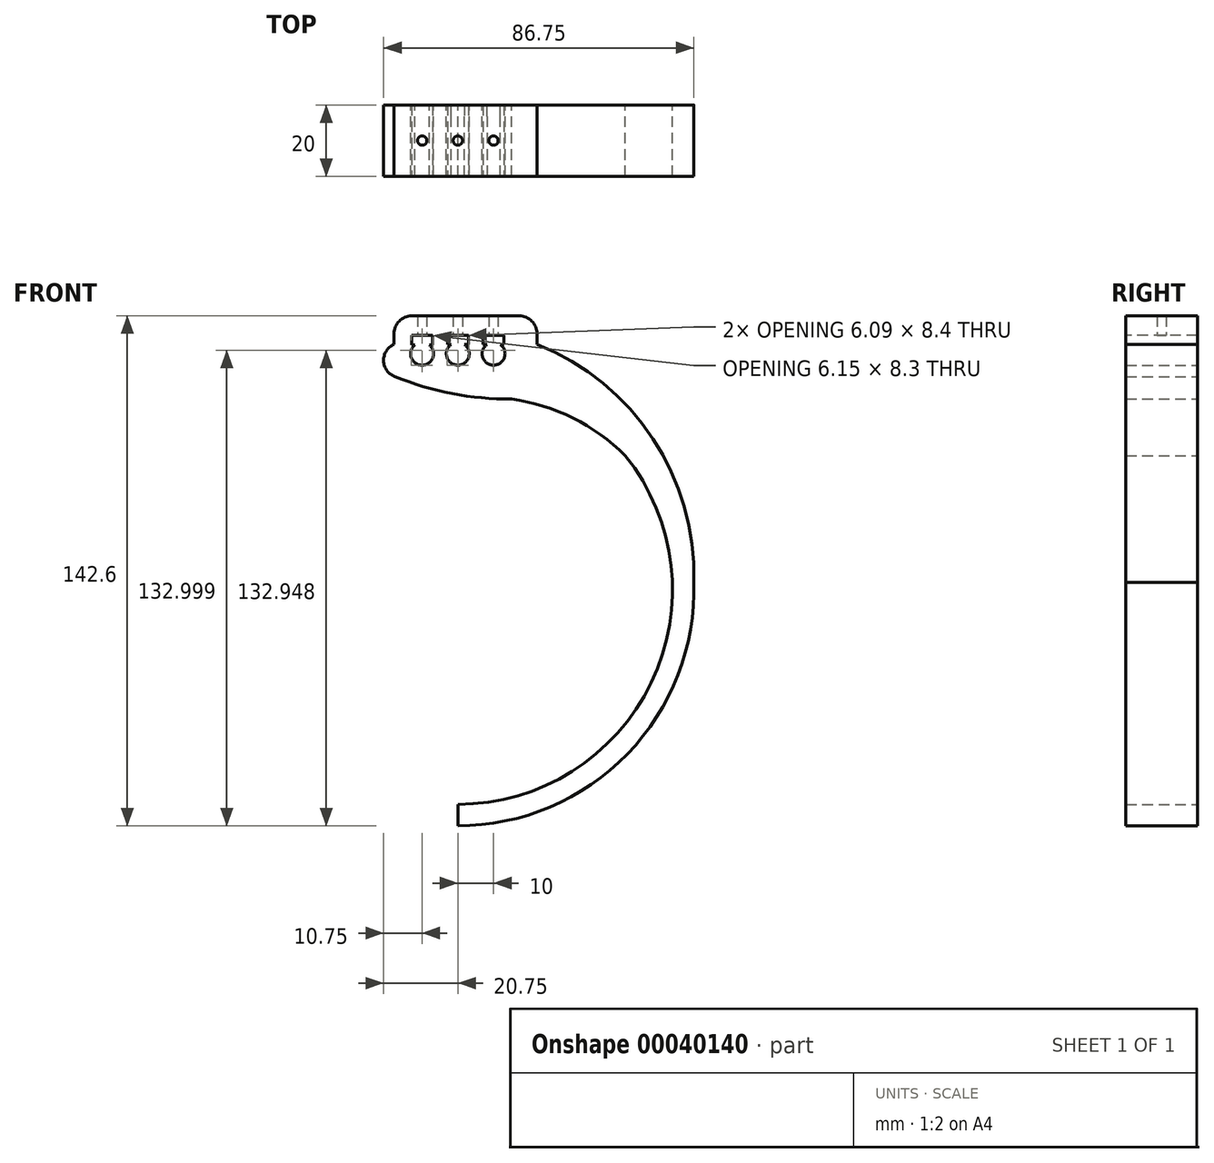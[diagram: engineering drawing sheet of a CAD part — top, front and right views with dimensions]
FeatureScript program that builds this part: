
annotation { "Feature Type Name" : "Feature", "Feature Type Description" : "" }
export const myFeature = defineFeature(function(context is Context, id is Id, definition is map)
    precondition{}
    {
        {
            var Q0;
            Q0=qCreatedBy(makeId("Front.planeOp"),FACE);
            var sketch = newSketch(context, id + "F0", { "sketchPlane" : qUnion([Q0])});
            skArc(sketch, "E0", {"start": v(0, -132) * mm, "mid": v(47.4, -111.93) * mm, "end": v(65.97, -63.94) * mm});
            skPoint(sketch, "E0.first.point", {"position": v(0, 0) * mm});
            skPoint(sketch, "E0.second.point", {"position": v(0, -132) * mm});
            skPoint(sketch, "E0.third.point", {"position": v(-62.47, -87.29) * mm});
            skArc(sketch, "E1", {"start": v(0, -126) * mm, "mid": v(54.09, -91.97) * mm, "end": v(46.83, -28.49) * mm});
            skLineSegment(sketch, "E2", {"start": v(0, -132) * mm, "end": v(0, -126) * mm});
            skPoint(sketch, "E3", {"position": v(19.17, -2.85) * mm});
            skPoint(sketch, "E4", {"position": v(13.26, -7.48) * mm});
            skPoint(sketch, "E5.end.orphan", {"position": v(0, -6) * mm});
            skPoint(sketch, "E6.end.orphan", {"position": v(-14.54, -4) * mm});
            skPoint(sketch, "E7.first.point", {"position": v(-10, 0) * mm});
            skArc(sketch, "E8", {"start": v(11.87, -2.6) * mm, "mid": v(12.85, -1.46) * mm, "end": v(13.2, 0) * mm});
            skPoint(sketch, "E9.end.orphan", {"position": v(10.73, -4) * mm});
            skPoint(sketch, "E10", {"position": v(48.2, -21.54) * mm});
            skArc(sketch, "E11", {"start": v(46.83, -28.49) * mm, "mid": v(32.2, -17.97) * mm, "end": v(15, -12.66) * mm});
            skArc(sketch, "E12", {"start": v(1.87, -2.6) * mm, "mid": v(3.2, 0) * mm, "end": v(1.87, 2.6) * mm});
            skArc(sketch, "E13", {"start": v(65.97, -63.94) * mm, "mid": v(54.56, -23.75) * mm, "end": v(22.14, 2.6) * mm});
            skArc(sketch, "E14.MirrorCS", {"start": v(1.87, 2.6) * mm, "mid": v(0, -3.2) * mm, "end": v(-1.87, 2.6) * mm});
            skArc(sketch, "E15.MirrorCS", {"start": v(11.87, 2.6) * mm, "mid": v(10, -3.2) * mm, "end": v(8.14, 2.6) * mm});
            skPoint(sketch, "E16.end.orphan", {"position": v(15, -2.66) * mm});
            skArc(sketch, "E17", {"start": v(-17.56, -6.38) * mm, "mid": v(-1.6, -11.13) * mm, "end": v(15, -12.66) * mm});
            skPoint(sketch, "E18.end.orphan", {"position": v(-16.98, -2.62) * mm});
            skArc(sketch, "E19.trimOffspring", {"start": v(-1.87, 2.6) * mm, "mid": v(-3.2, 0) * mm, "end": v(-1.87, -2.6) * mm});
            skArc(sketch, "E20.trimOffspring", {"start": v(6.8, 0) * mm, "mid": v(7.16, -1.46) * mm, "end": v(8.14, -2.6) * mm});
            skPoint(sketch, "E21.start.orphan", {"position": v(-8.13, -2.6) * mm});
            skPoint(sketch, "E22.trimOffspring.end.orphan", {"position": v(-11.84, -2.62) * mm});
            skArc(sketch, "E23", {"start": v(-11.84, 2.62) * mm, "mid": v(-10.01, -3.2) * mm, "end": v(-8.13, 2.6) * mm});
            skPoint(sketch, "E24.start.orphan", {"position": v(-16.98, 2.62) * mm});
            skLineSegment(sketch, "E25", {"start": v(22.14, 2.6) * mm, "end": v(11.87, 2.6) * mm});
            skLineSegment(sketch, "E26", {"start": v(8.14, 2.6) * mm, "end": v(1.87, 2.6) * mm});
            skLineSegment(sketch, "E27", {"start": v(-1.87, 2.6) * mm, "end": v(-8.13, 2.6) * mm});
            skLineSegment(sketch, "E28", {"start": v(-11.84, 2.62) * mm, "end": v(-17.86, 2.62) * mm});
            skArc(sketch, "E29", {"start": v(-17.86, 2.62) * mm, "mid": v(-20.75, -1.98) * mm, "end": v(-17.56, -6.38) * mm});
            skSolve(sketch);
        }
        {
            var Q0;
            Q0 = qSketchRegion(id + "F0", true);
            extrude(context, id + "F1", {"entities" : qUnion([Q0]), "depth" : 16.8 * mm, "hasSecondDirection" : true, "secondDirectionOppositeDirection" : true, "secondDirectionDepth" : 3.2 * mm});
        }
        {
            var Q0;
            Q0=makeQuery(id+"F1.opExtrude","SWEPT_FACE",FACE,{"disambiguationData":[OSD([sQuery(id+"F0.wireOp",EDGE,"E25")])]});
            var sketch = newSketch(context, id + "F2", { "sketchPlane" : qUnion([Q0])});
            skLineSegment(sketch, "E30.bottom", {"start": v(22.14, 3.2) * mm, "end": v(-17.86, 3.2) * mm});
            skLineSegment(sketch, "E30.top", {"start": v(22.14, -16.8) * mm, "end": v(-17.86, -16.8) * mm});
            skLineSegment(sketch, "E30.left", {"start": v(22.14, 3.2) * mm, "end": v(22.14, -16.8) * mm});
            skLineSegment(sketch, "E30.right", {"start": v(-17.86, 3.2) * mm, "end": v(-17.86, -16.8) * mm});
            skCircle(sketch, "E31", {"center": v(-9.95, -6.8) * mm, "radius": 1.3 * mm});
            skCircle(sketch, "E32", {"center": v(0, -6.8) * mm, "radius": 1.3 * mm});
            skCircle(sketch, "E33", {"center": v(9.98, -6.8) * mm, "radius": 1.3 * mm});
            skSolve(sketch);
        }
        {
            var Q0;
            Q0 = qSketchRegion(id + "F2", true);
            extrude(context, id + "F3", {"entities" : qUnion([Q0]), "operationType" : NewBodyOperationType.ADD, "depth" : 8 * mm});
        }
        {
            var Q0;
            Q0=makeQuery(id+"F1.opExtrude","CAP_FACE",FACE,{"disambiguationData":[OSD([sQuery(id+"F0.wireOp",EDGE,"E0"),sQuery(id+"F0.wireOp",EDGE,"E1"),sQuery(id+"F0.wireOp",EDGE,"E2"),sQuery(id+"F0.wireOp",EDGE,"0a2bbde4-e674-40ac-8c8a-23e3a44a7db3"),sQuery(id+"F0.wireOp",EDGE,"E11"),sQuery(id+"F0.wireOp",EDGE,"E13"),sQuery(id+"F0.wireOp",EDGE,"E14.MirrorCS"),sQuery(id+"F0.wireOp",EDGE,"3cbbe4b5-725f-413c-9702-e79f386d2b464.MirrorCS"),sQuery(id+"F0.wireOp",EDGE,"E15.MirrorCS"),sQuery(id+"F0.wireOp",EDGE,"3cbbe4b5-725f-413c-9702-e79f386d2b467.MirrorCS"),sQuery(id+"F0.wireOp",EDGE,"3cbbe4b5-725f-413c-9702-e79f386d2b468.MirrorCS"),sQuery(id+"F0.wireOp",EDGE,"E17"),sQuery(id+"F0.wireOp",EDGE,"a40e079f-89b8-40f5-868c-d61c1e4f2035"),sQuery(id+"F0.wireOp",EDGE,"E24"),sQuery(id+"F0.wireOp",EDGE,"E19.trimOffspring"),sQuery(id+"F0.wireOp",EDGE,"E20.trimOffspring"),sQuery(id+"F0.wireOp",EDGE,"E23")])],"isStart":true});
            var sketch = newSketch(context, id + "F4", { "sketchPlane" : qUnion([Q0])});
            skCircle(sketch, "E34", {"center": v(0, 0) * mm, "radius": 3.2 * mm});
            skCircle(sketch, "E35", {"center": v(-10, 0) * mm, "radius": 3.2 * mm});
            skCircle(sketch, "E36", {"center": v(10, 0) * mm, "radius": 3.2 * mm});
            skSolve(sketch);
        }
        {
            var Q0;
            Q0 = qSketchRegion(id + "F4", true);
            extrude(context, id + "F5", {"entities" : qUnion([Q0]), "operationType" : NewBodyOperationType.REMOVE, "oppositeDirection" : true, "depth" : 3.2 * mm});
        }
        {
            var Q0;
            Q0=makeQuery(id+"F3.opExtrude","CAP_EDGE",EDGE,{"disambiguationData":[OSD([sQuery(id+"F2.wireOp",EDGE,"E30.left")])],"isStart":false});
            var Q1;
            Q1=makeQuery(id+"F3.opExtrude","CAP_EDGE",EDGE,{"disambiguationData":[OSD([sQuery(id+"F2.wireOp",EDGE,"E30.right")])],"isStart":false});
            fillet(context, id + "F6", {"entities" : qUnion([Q0, Q1]), "radius" : 5 * mm, "tangentPropagation" : true, "allowEdgeOverflow" : false});
        }
        {
            var Q0;
            Q0=makeQuery(id+"F3.boolean.opBoolean","MERGE",FACE,{"derivedFrom":[makeQuery(id+"F1.opExtrude","CAP_FACE",FACE,{"disambiguationData":[OSD([sQuery(id+"F0.wireOp",EDGE,"E0"),sQuery(id+"F0.wireOp",EDGE,"E1"),sQuery(id+"F0.wireOp",EDGE,"E2"),sQuery(id+"F0.wireOp",EDGE,"E11"),sQuery(id+"F0.wireOp",EDGE,"E13"),sQuery(id+"F0.wireOp",EDGE,"E14.MirrorCS"),sQuery(id+"F0.wireOp",EDGE,"E15.MirrorCS"),sQuery(id+"F0.wireOp",EDGE,"E17"),sQuery(id+"F0.wireOp",EDGE,"E19.trimOffspring"),sQuery(id+"F0.wireOp",EDGE,"E23"),sQuery(id+"F0.wireOp",EDGE,"E25"),sQuery(id+"F0.wireOp",EDGE,"E26"),sQuery(id+"F0.wireOp",EDGE,"E27"),sQuery(id+"F0.wireOp",EDGE,"E28"),sQuery(id+"F0.wireOp",EDGE,"E29")])],"isStart":false}),makeQuery(id+"F3.opExtrude","SWEPT_FACE",FACE,{"disambiguationData":[OSD([sQuery(id+"F2.wireOp",EDGE,"E30.top")])]})]});
            var sketch = newSketch(context, id + "F7", { "sketchPlane" : qUnion([Q0])});
            skLineSegment(sketch, "E37.rect.bottom", {"start": v(2.92, 2.6) * mm, "end": v(-2.92, 2.6) * mm});
            skLineSegment(sketch, "E37.rect.top", {"start": v(2.92, 5.2) * mm, "end": v(-2.92, 5.2) * mm});
            skLineSegment(sketch, "E37.rect.left", {"start": v(2.92, 2.6) * mm, "end": v(2.92, 5.2) * mm});
            skLineSegment(sketch, "E37.rect.right", {"start": v(-2.92, 2.6) * mm, "end": v(-2.92, 5.2) * mm});
            skPoint(sketch, "E37.rect.middle", {"position": v(0, 3.9) * mm});
            skLineSegment(sketch, "E38.rect.bottom", {"start": v(-7.08, 2.5) * mm, "end": v(-12.92, 2.5) * mm});
            skLineSegment(sketch, "E38.rect.top", {"start": v(-7.08, 5.1) * mm, "end": v(-12.92, 5.1) * mm});
            skLineSegment(sketch, "E38.rect.left", {"start": v(-7.08, 2.5) * mm, "end": v(-7.08, 5.1) * mm});
            skLineSegment(sketch, "E38.rect.right", {"start": v(-12.92, 2.5) * mm, "end": v(-12.92, 5.1) * mm});
            skPoint(sketch, "E38.rect.middle", {"position": v(-10, 3.8) * mm});
            skLineSegment(sketch, "E39.rect.bottom", {"start": v(12.92, 2.6) * mm, "end": v(7.08, 2.6) * mm});
            skLineSegment(sketch, "E39.rect.top", {"start": v(12.92, 5.2) * mm, "end": v(7.08, 5.2) * mm});
            skLineSegment(sketch, "E39.rect.left", {"start": v(12.92, 2.6) * mm, "end": v(12.92, 5.2) * mm});
            skLineSegment(sketch, "E39.rect.right", {"start": v(7.08, 2.6) * mm, "end": v(7.08, 5.2) * mm});
            skPoint(sketch, "E39.rect.middle", {"position": v(10, 3.9) * mm});
            skSolve(sketch);
        }
        {
            var Q0;
            Q0 = qSketchRegion(id + "F7", true);
            extrude(context, id + "F8", {"entities" : qUnion([Q0]), "operationType" : NewBodyOperationType.REMOVE, "oppositeDirection" : true, "depth" : 25 * mm});
        }
    });
